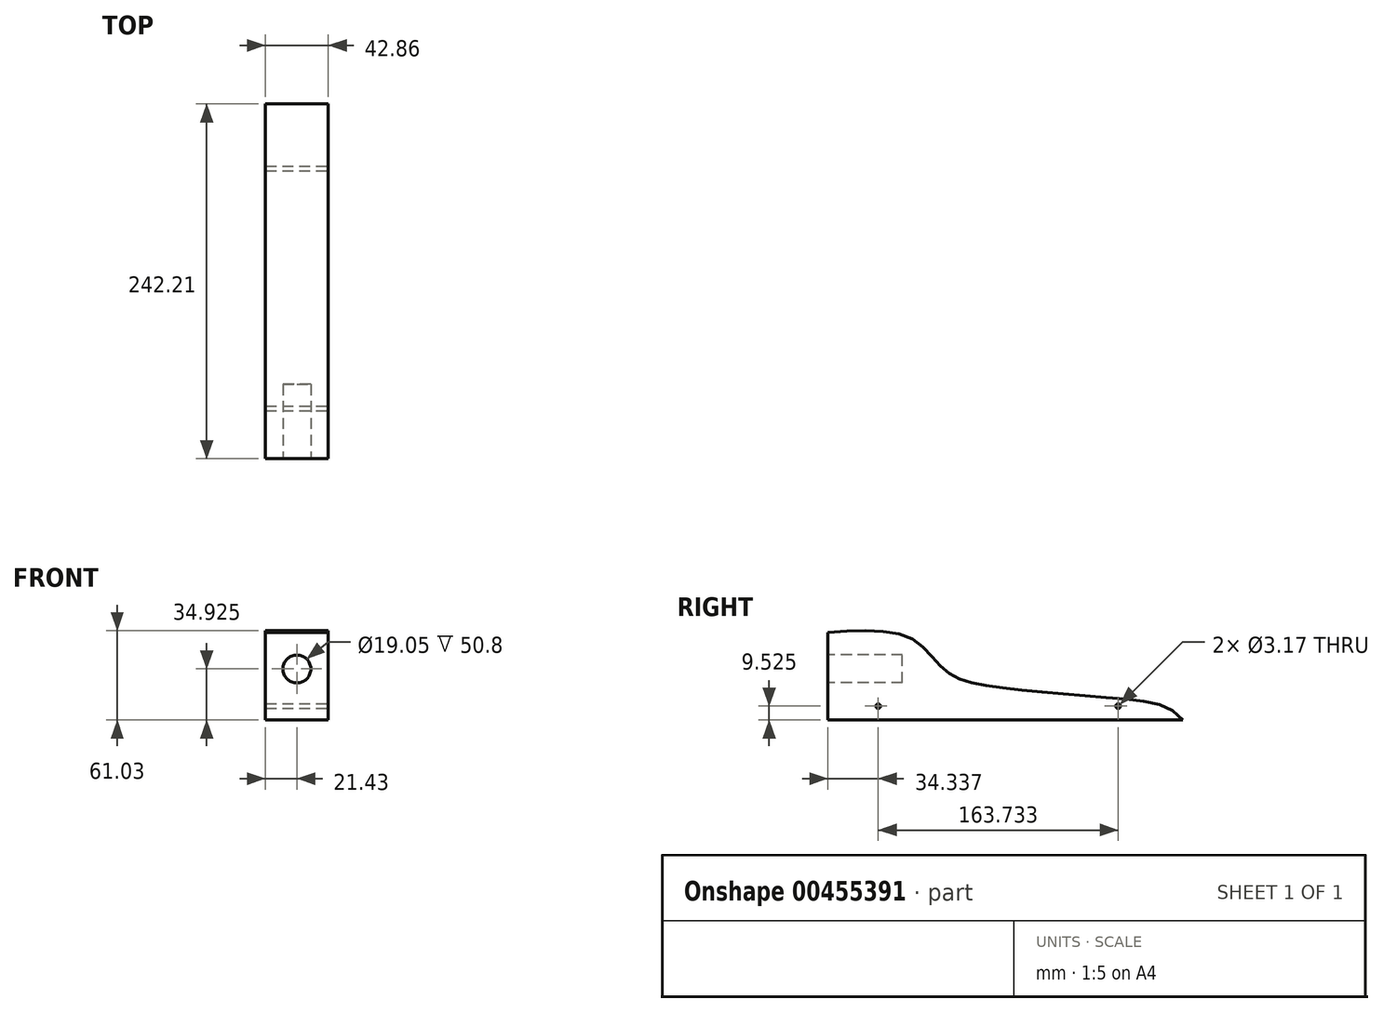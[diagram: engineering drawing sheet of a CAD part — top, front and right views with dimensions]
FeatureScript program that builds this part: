
annotation { "Feature Type Name" : "Feature", "Feature Type Description" : "" }
export const myFeature = defineFeature(function(context is Context, id is Id, definition is map)
    precondition{}
    {
        {
            var Q0;
            Q0=qCreatedBy(makeId("Right.planeOp"),FACE);
            var sketch = newSketch(context, id + "F0", { "sketchPlane" : qUnion([Q0])});
            skLineSegment(sketch, "E0", {"start": v(-152.4, 0) * mm, "end": v(152.4, 0) * mm});
            skLineSegment(sketch, "E1", {"start": v(-152.4, 0) * mm, "end": v(-152.4, 69.85) * mm});
            skLineSegment(sketch, "E2", {"start": v(152.4, 0) * mm, "end": v(152.4, 19.05) * mm});
            skLineSegment(sketch, "E3", {"start": v(152.4, 19.05) * mm, "end": v(-152.4, 69.85) * mm});
            skPoint(sketch, "E4.endSnap0", {"position": v(-152.4, 34.93) * mm});
            skLineSegment(sketch, "E5.0", {"start": v(-95.25, 50.8) * mm, "end": v(-152.4, 50.8) * mm, "construction": true});
            skLineSegment(sketch, "E5.1", {"start": v(-95.25, 50.8) * mm, "end": v(-95.25, 19.05) * mm, "construction": true});
            skLineSegment(sketch, "E5.2", {"start": v(-95.25, 19.05) * mm, "end": v(-152.4, 19.05) * mm, "construction": true});
            skSolve(sketch);
        }
        {
            var Q0;
            Q0=makeQuery(id+"F0.imprint","IMPRINT",FACE,{"disambiguationData":[TD([[makeQuery(id+"F0.imprint","IMPRINT",EDGE,{"derivedFrom":sQuery(id+"F0.wireOp",EDGE,"E0")}),1.0]])]});
            extrude(context, id + "F1", {"entities" : qUnion([Q0]), "depth" : 42.86 * mm, "symmetric" : true});
        }
        {
            var Q0;
            Q0=makeQuery(id+"F1.opExtrude","SWEPT_FACE",FACE,{"disambiguationData":[OSD([sQuery(id+"F0.wireOp",EDGE,"E1")])]});
            var sketch = newSketch(context, id + "F2", { "sketchPlane" : qUnion([Q0])});
            skLineSegment(sketch, "E6", {"start": v(21.43, 34.93) * mm, "end": v(0, 34.93) * mm, "construction": true});
            skCircle(sketch, "E7", {"center": v(0, 34.93) * mm, "radius": 9.53 * mm});
            skSolve(sketch);
        }
        {
            var Q0;
            Q0=makeQuery(id+"F2.imprint","IMPRINT",FACE,{"disambiguationData":[TD([[makeQuery(id+"F2.imprint","IMPRINT",EDGE,{"derivedFrom":sQuery(id+"F2.wireOp",EDGE,"E7")}),1.0]])]});
            var Q1;
            Q1=sQuery(id+"F2.wireOp",EDGE,"E7");
            extrude(context, id + "F3", {"entities" : qUnion([Q0]), "operationType" : NewBodyOperationType.REMOVE, "surfaceEntities" : qUnion([Q1]), "oppositeDirection" : true, "depth" : 50.8 * mm});
        }
        {
            var Q0;
            Q0=makeQuery(id+"F1.opExtrude","CAP_FACE",FACE,{"disambiguationData":[OSD([sQuery(id+"F0.wireOp",EDGE,"E0"),sQuery(id+"F0.wireOp",EDGE,"E1"),sQuery(id+"F0.wireOp",EDGE,"E2"),sQuery(id+"F0.wireOp",EDGE,"E3")])],"isStart":false});
            var sketch = newSketch(context, id + "F4", { "sketchPlane" : qUnion([Q0])});
            skLineSegment(sketch, "E8", {"start": v(-152.4, 34.93) * mm, "end": v(-152.4, 44.45) * mm, "construction": true});
            skLineSegment(sketch, "E9.0", {"start": v(-95.25, 19.05) * mm, "end": v(-152.4, 19.05) * mm, "construction": true});
            skLineSegment(sketch, "E9.1", {"start": v(-95.25, 50.8) * mm, "end": v(-95.25, 19.05) * mm, "construction": true});
            skLineSegment(sketch, "E9.2", {"start": v(-152.4, 50.8) * mm, "end": v(-95.25, 50.8) * mm, "construction": true});
            skLineSegment(sketch, "E10", {"start": v(57.15, 0) * mm, "end": v(57.15, 34.93) * mm, "construction": true});
            skLineSegment(sketch, "E11", {"start": v(-152.4, 44.45) * mm, "end": v(-101.6, 44.45) * mm, "construction": true});
            skLineSegment(sketch, "E12", {"start": v(-101.6, 44.45) * mm, "end": v(-101.6, 25.4) * mm, "construction": true});
            skLineSegment(sketch, "E13", {"start": v(-101.6, 25.4) * mm, "end": v(-152.4, 25.4) * mm, "construction": true});
            skPoint(sketch, "E14.1.internal.orphan", {"position": v(152.4, 9.53) * mm});
            skFitSpline(sketch, "E15", {"points": [v(-152.4, 59.9) * mm, v(-95.25, 55.49) * mm, v(-71.9, 33.45) * mm, v(-39.29, 22.88) * mm, v(43.1, 14.95) * mm, v(89.81, 0) * mm, v(98.83, -11.98) * mm], "startDerivative": vector(332.59, 21.27) * mm, "endDerivative": vector(50.63, 136.33) * mm});
            skCircle(sketch, "E16", {"center": v(-118.06, 9.53) * mm, "radius": 1.59 * mm});
            skCircle(sketch, "E17", {"center": v(45.67, 9.53) * mm, "radius": 1.59 * mm});
            skSolve(sketch);
        }
        {
            var Q0;
            Q0=makeQuery(id+"F4.imprint","IMPRINT",FACE,{"disambiguationData":[TD([[makeQuery(id+"F4.imprint","IMPRINT",EDGE,{"derivedFrom":sQuery(id+"F4.wireOp",EDGE,"E16")}),-1.0]])]});
            extrude(context, id + "F5", {"entities" : qUnion([Q0]), "operationType" : NewBodyOperationType.INTERSECT, "endBound" : BoundingType.THROUGH_ALL, "oppositeDirection" : true, "depth" : 25.4 * mm});
        }
    });
